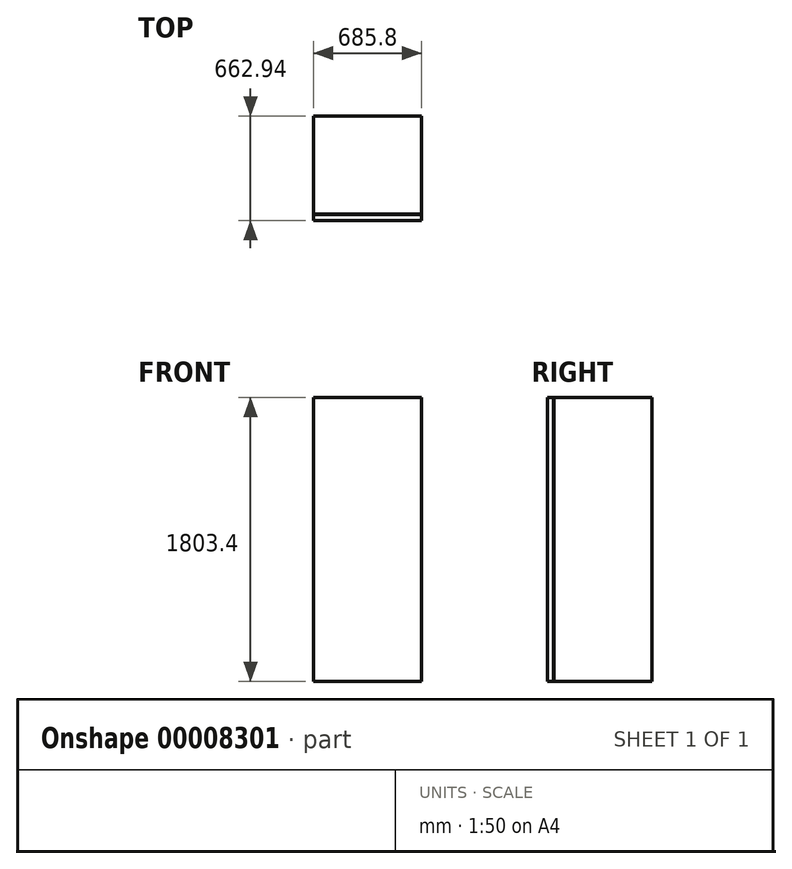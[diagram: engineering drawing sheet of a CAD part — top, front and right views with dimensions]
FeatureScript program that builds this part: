
annotation { "Feature Type Name" : "Feature", "Feature Type Description" : "" }
export const myFeature = defineFeature(function(context is Context, id is Id, definition is map)
    precondition{}
    {
        {
            var Q0;
            Q0=qCreatedBy(makeId("Top.planeOp"),FACE);
            var sketch = newSketch(context, id + "F0", { "sketchPlane" : qUnion([Q0])});
            skLineSegment(sketch, "E0.bottom", {"start": v(-17.93, 621.31) * mm, "end": v(667.87, 621.31) * mm});
            skLineSegment(sketch, "E0.top", {"start": v(-17.93, -0.99) * mm, "end": v(667.87, -0.99) * mm});
            skLineSegment(sketch, "E0.left", {"start": v(-17.93, 621.31) * mm, "end": v(-17.93, -0.99) * mm});
            skLineSegment(sketch, "E0.right", {"start": v(667.87, 621.31) * mm, "end": v(667.87, -0.99) * mm});
            skLineSegment(sketch, "E1.bottom", {"start": v(-17.93, -3.53) * mm, "end": v(667.87, -3.53) * mm});
            skLineSegment(sketch, "E1.top", {"start": v(-17.93, -41.63) * mm, "end": v(667.87, -41.63) * mm});
            skLineSegment(sketch, "E1.left", {"start": v(-17.93, -3.53) * mm, "end": v(-17.93, -41.63) * mm});
            skLineSegment(sketch, "E1.right", {"start": v(667.87, -3.53) * mm, "end": v(667.87, -41.63) * mm});
            skLineSegment(sketch, "E2", {"start": v(-20.97, -0.99) * mm, "end": v(-20.97, -3.53) * mm, "construction": true});
            skSolve(sketch);
        }
        {
            var Q0;
            Q0 = qSketchRegion(id + "F0", true);
            extrude(context, id + "F1", {"entities" : qUnion([Q0]), "depth" : 1803.4 * mm});
        }
    });
